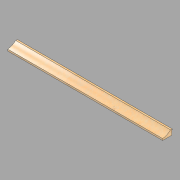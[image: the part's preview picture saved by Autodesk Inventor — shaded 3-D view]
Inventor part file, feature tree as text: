
AUTODESK INVENTOR PART (.ipt)
format: ipt  version: 2022.2 (Build 262287010, 287A)  size: 121,856 bytes
history: native  units: in
note: dims shown in document units (in); Inventor stores cm internally (conversion verified against a paired STEP export)
features: revolve x2, direct_edit x1, other x1
ambient origin geometry x8: Origin, YZ Plane, XZ Plane, XY Plane, X Axis, Y Axis, Z Axis, Center Point
bodies: Solid1 (feature_tree)
feature tree (4):
  direct_edit  "Direct Edit1"
  other  "Jamb (lower) (1)"
  revolve  "Rotate1"  [1 undecoded]
  revolve  "Rotate2"  [1 undecoded]
note: 2 required parameter values undecoded (feature->parameter linkage not recoverable at this tier; creation-order binding heuristic only, values carry confidence <= 0.55)
